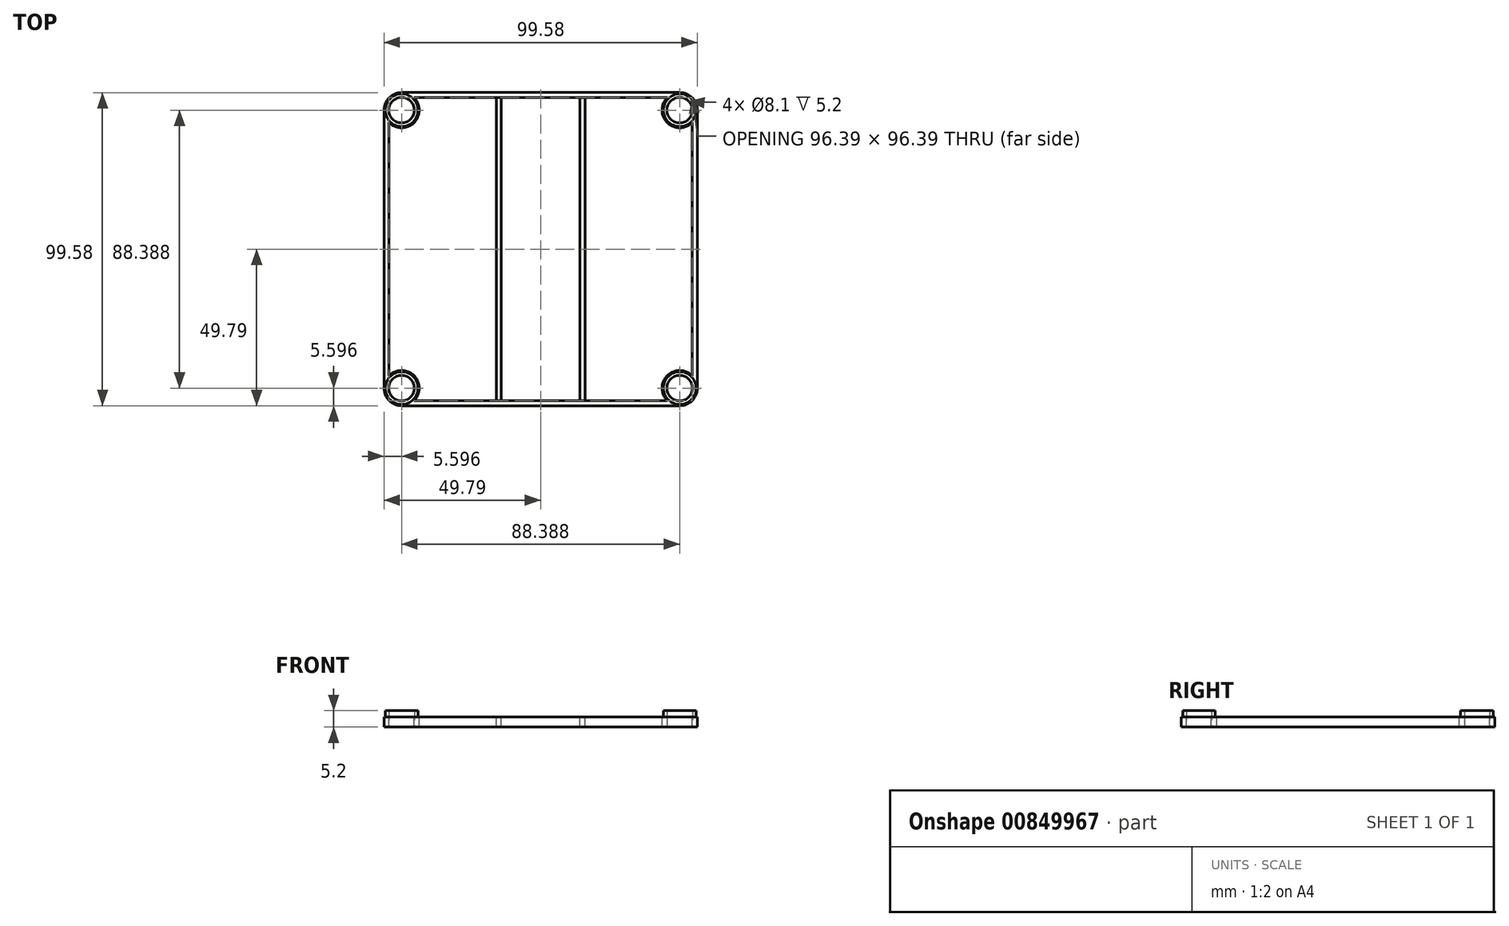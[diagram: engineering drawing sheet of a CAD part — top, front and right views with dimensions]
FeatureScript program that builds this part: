
annotation { "Feature Type Name" : "Feature", "Feature Type Description" : "" }
export const myFeature = defineFeature(function(context is Context, id is Id, definition is map)
    precondition{}
    {
        {
            var Q0;
            Q0=qCreatedBy(makeId("Top.planeOp"),FACE);
            var sketch = newSketch(context, id + "F0", { "sketchPlane" : qUnion([Q0])});
            skLineSegment(sketch, "E0.bottom", {"start": v(44.2, 44.2) * mm, "end": v(-44.2, 44.2) * mm, "construction": true});
            skLineSegment(sketch, "E0.top", {"start": v(44.2, -44.2) * mm, "end": v(-44.2, -44.2) * mm, "construction": true});
            skLineSegment(sketch, "E0.left", {"start": v(44.2, 44.2) * mm, "end": v(44.2, -44.2) * mm, "construction": true});
            skLineSegment(sketch, "E0.right", {"start": v(-44.2, 44.2) * mm, "end": v(-44.2, -44.2) * mm, "construction": true});
            skPoint(sketch, "E0.middle", {"position": v(0, 0) * mm});
            skLineSegment(sketch, "E1", {"start": v(-44.2, -44.2) * mm, "end": v(44.2, 44.2) * mm, "construction": true});
            skCircle(sketch, "E2", {"center": v(44.2, 44.2) * mm, "radius": 4 * mm, "construction": true});
            skCircle(sketch, "E3", {"center": v(-44.2, 44.2) * mm, "radius": 4 * mm, "construction": true});
            skCircle(sketch, "E4", {"center": v(-44.2, -44.2) * mm, "radius": 4 * mm, "construction": true});
            skCircle(sketch, "E5", {"center": v(44.2, -44.2) * mm, "radius": 4 * mm, "construction": true});
            skCircle(sketch, "E6", {"center": v(44.2, 44.2) * mm, "radius": 32.5 * mm, "construction": true});
            skCircle(sketch, "E7", {"center": v(-44.2, 44.2) * mm, "radius": 32.5 * mm, "construction": true});
            skCircle(sketch, "E8", {"center": v(-44.2, -44.2) * mm, "radius": 32.5 * mm, "construction": true});
            skCircle(sketch, "E9", {"center": v(44.2, -44.2) * mm, "radius": 32.5 * mm, "construction": true});
            skSolve(sketch);
        }
        {
            var Q0;
            Q0=qCreatedBy(makeId("Front.planeOp"),FACE);
            var sketch = newSketch(context, id + "F1", { "sketchPlane" : qUnion([Q0])});
            skLineSegment(sketch, "E10", {"start": v(0, 0) * mm, "end": v(0, 0.6) * mm});
            skLineSegment(sketch, "E11", {"start": v(0, 0.6) * mm, "end": v(0, 3.2) * mm});
            skLineSegment(sketch, "E12", {"start": v(0, 3.2) * mm, "end": v(0, 5.2) * mm});
            skSolve(sketch);
        }
        {
            var Q0;
            Q0=qCreatedBy(makeId("Top.planeOp"),FACE);
            var sketch = newSketch(context, id + "F2", { "sketchPlane" : qUnion([Q0])});
            skCircle(sketch, "E13.0", {"center": v(44.2, 44.2) * mm, "radius": 5.6 * mm, "construction": true});
            skPoint(sketch, "E14.center", {"position": v(0, 0) * mm});
            skLineSegment(sketch, "E15", {"start": v(44.2, 49.8) * mm, "end": v(0, 49.8) * mm});
            skLineSegment(sketch, "E16", {"start": v(49.8, 44.2) * mm, "end": v(49.8, 0) * mm});
            skArc(sketch, "E17", {"start": v(44.2, 49.8) * mm, "mid": v(48.15, 48.15) * mm, "end": v(49.8, 44.2) * mm});
            skCircle(sketch, "E18.0", {"center": v(44.2, 44.2) * mm, "radius": 4 * mm, "construction": true});
            skLineSegment(sketch, "E19", {"start": v(44.2, 48.2) * mm, "end": v(40.27, 48.2) * mm, "construction": true});
            skLineSegment(sketch, "E20", {"start": v(48.2, 44.2) * mm, "end": v(48.2, 40.27) * mm, "construction": true});
            skLineSegment(sketch, "E21", {"start": v(40.27, 48.2) * mm, "end": v(0, 48.2) * mm});
            skLineSegment(sketch, "E22", {"start": v(48.2, 40.27) * mm, "end": v(48.2, 0) * mm});
            skArc(sketch, "E23", {"start": v(40.27, 48.2) * mm, "mid": v(40.23, 40.23) * mm, "end": v(48.2, 40.27) * mm});
            skArc(sketch, "E24.1.0", {"start": v(-48.2, 40.27) * mm, "mid": v(-40.23, 40.23) * mm, "end": v(-40.27, 48.2) * mm});
            skLineSegment(sketch, "E24.1.1", {"start": v(-48.2, 40.27) * mm, "end": v(-48.2, 0) * mm});
            skLineSegment(sketch, "E24.1.2", {"start": v(-49.8, 44.2) * mm, "end": v(-49.8, 0) * mm});
            skLineSegment(sketch, "E24.1.3", {"start": v(-40.27, 48.2) * mm, "end": v(0, 48.2) * mm});
            skLineSegment(sketch, "E24.1.4", {"start": v(-44.2, 49.8) * mm, "end": v(0, 49.8) * mm});
            skArc(sketch, "E24.1.5", {"start": v(-49.8, 44.2) * mm, "mid": v(-48.15, 48.15) * mm, "end": v(-44.2, 49.8) * mm});
            skArc(sketch, "E24.2.0", {"start": v(-40.27, -48.2) * mm, "mid": v(-40.23, -40.23) * mm, "end": v(-48.2, -40.27) * mm});
            skLineSegment(sketch, "E24.2.1", {"start": v(-40.27, -48.2) * mm, "end": v(0, -48.2) * mm});
            skLineSegment(sketch, "E24.2.2", {"start": v(-44.2, -49.8) * mm, "end": v(0, -49.8) * mm});
            skLineSegment(sketch, "E24.2.3", {"start": v(-48.2, -40.27) * mm, "end": v(-48.2, 0) * mm});
            skLineSegment(sketch, "E24.2.4", {"start": v(-49.8, -44.2) * mm, "end": v(-49.8, 0) * mm});
            skArc(sketch, "E24.2.5", {"start": v(-44.2, -49.8) * mm, "mid": v(-48.15, -48.15) * mm, "end": v(-49.8, -44.2) * mm});
            skArc(sketch, "E24.3.0", {"start": v(48.2, -40.27) * mm, "mid": v(40.23, -40.23) * mm, "end": v(40.27, -48.2) * mm});
            skLineSegment(sketch, "E24.3.1", {"start": v(48.2, -40.27) * mm, "end": v(48.2, 0) * mm});
            skLineSegment(sketch, "E24.3.2", {"start": v(49.8, -44.2) * mm, "end": v(49.8, 0) * mm});
            skLineSegment(sketch, "E24.3.3", {"start": v(40.27, -48.2) * mm, "end": v(0, -48.2) * mm});
            skLineSegment(sketch, "E24.3.4", {"start": v(44.2, -49.8) * mm, "end": v(0, -49.8) * mm});
            skArc(sketch, "E24.3.5", {"start": v(49.8, -44.2) * mm, "mid": v(48.15, -48.15) * mm, "end": v(44.2, -49.8) * mm});
            skSolve(sketch);
        }
        {
            var Q0;
            Q0=qCreatedBy(makeId("Top.planeOp"),FACE);
            var sketch = newSketch(context, id + "F3", { "sketchPlane" : qUnion([Q0])});
            skLineSegment(sketch, "E25.0.0", {"start": v(0, -48.2) * mm, "end": v(40.27, -48.2) * mm, "construction": true});
            skArc(sketch, "E25.0.1", {"start": v(40.27, -48.2) * mm, "mid": v(40.23, -40.23) * mm, "end": v(48.2, -40.27) * mm, "construction": true});
            skLineSegment(sketch, "E25.0.2", {"start": v(48.2, -40.27) * mm, "end": v(48.2, 0) * mm, "construction": true});
            skLineSegment(sketch, "E25.0.3", {"start": v(48.2, 0) * mm, "end": v(48.2, 40.27) * mm, "construction": true});
            skArc(sketch, "E25.0.4", {"start": v(48.2, 40.27) * mm, "mid": v(40.23, 40.23) * mm, "end": v(40.27, 48.2) * mm, "construction": true});
            skLineSegment(sketch, "E25.0.5", {"start": v(40.27, 48.2) * mm, "end": v(0, 48.2) * mm, "construction": true});
            skLineSegment(sketch, "E25.0.6", {"start": v(0, 48.2) * mm, "end": v(-40.27, 48.2) * mm, "construction": true});
            skArc(sketch, "E25.0.7", {"start": v(-40.27, 48.2) * mm, "mid": v(-40.23, 40.23) * mm, "end": v(-48.2, 40.27) * mm, "construction": true});
            skLineSegment(sketch, "E25.0.8", {"start": v(-48.2, 40.27) * mm, "end": v(-48.2, 0) * mm, "construction": true});
            skLineSegment(sketch, "E25.0.9", {"start": v(-48.2, 0) * mm, "end": v(-48.2, -40.27) * mm, "construction": true});
            skArc(sketch, "E25.0.10", {"start": v(-48.2, -40.27) * mm, "mid": v(-40.23, -40.23) * mm, "end": v(-40.27, -48.2) * mm, "construction": true});
            skLineSegment(sketch, "E25.0.11", {"start": v(-40.27, -48.2) * mm, "end": v(0, -48.2) * mm, "construction": true});
            skLineSegment(sketch, "E26.bottom", {"start": v(12.5, 48.2) * mm, "end": v(-12.5, 48.2) * mm});
            skLineSegment(sketch, "E26.top", {"start": v(12.5, -48.2) * mm, "end": v(-12.5, -48.2) * mm});
            skLineSegment(sketch, "E26.left", {"start": v(12.5, 48.2) * mm, "end": v(12.5, -48.2) * mm});
            skLineSegment(sketch, "E26.right", {"start": v(-12.5, 48.2) * mm, "end": v(-12.5, -48.2) * mm});
            skPoint(sketch, "E26.middle", {"position": v(0, 0) * mm});
            skLineSegment(sketch, "E27", {"start": v(-12.5, -48.2) * mm, "end": v(-14.1, -48.2) * mm});
            skLineSegment(sketch, "E28", {"start": v(-14.1, -48.2) * mm, "end": v(-14.1, 48.2) * mm});
            skLineSegment(sketch, "E29", {"start": v(-14.1, 48.2) * mm, "end": v(-12.5, 48.2) * mm});
            skLineSegment(sketch, "E30", {"start": v(12.5, 48.2) * mm, "end": v(14.1, 48.2) * mm});
            skLineSegment(sketch, "E31", {"start": v(14.1, 48.2) * mm, "end": v(14.1, -48.2) * mm});
            skLineSegment(sketch, "E32", {"start": v(14.1, -48.2) * mm, "end": v(12.5, -48.2) * mm});
            skSolve(sketch);
        }
        {
            var Q0;
            Q0=qCreatedBy(makeId("Top.planeOp"),FACE);
            var sketch = newSketch(context, id + "F4", { "sketchPlane" : qUnion([Q0])});
            skCircle(sketch, "E33.0", {"center": v(44.2, 44.2) * mm, "radius": 5.2 * mm});
            skCircle(sketch, "E34.1.0", {"center": v(-44.2, 44.2) * mm, "radius": 5.2 * mm});
            skCircle(sketch, "E34.2.0", {"center": v(-44.2, -44.2) * mm, "radius": 5.2 * mm});
            skCircle(sketch, "E34.3.0", {"center": v(44.2, -44.2) * mm, "radius": 5.2 * mm});
            skPoint(sketch, "E34.center", {"position": v(0, 0) * mm});
            skSolve(sketch);
        }
        {
            var Q0;
            Q0=qCreatedBy(makeId("Top.planeOp"),FACE);
            var sketch = newSketch(context, id + "F5", { "sketchPlane" : qUnion([Q0])});
            skCircle(sketch, "E35.0", {"center": v(44.2, 44.2) * mm, "radius": 4.05 * mm});
            skCircle(sketch, "E36.0", {"center": v(-44.2, 44.2) * mm, "radius": 4.05 * mm});
            skCircle(sketch, "E37.0", {"center": v(-44.2, -44.2) * mm, "radius": 4.05 * mm});
            skCircle(sketch, "E38.0", {"center": v(44.2, -44.2) * mm, "radius": 4.05 * mm});
            skSolve(sketch);
        }
        {
            var Q0;
            Q0 = qSketchRegion(id + "F2", true);
            var Q1;
            Q1=makeQuery(id+"F3.imprint","IMPRINT",FACE,{"disambiguationData":[TD([[makeQuery(id+"F3.imprint","IMPRINT",EDGE,{"derivedFrom":sQuery(id+"F3.wireOp",EDGE,"E26.right")}),-1.0]])]});
            var Q2;
            Q2=makeQuery(id+"F3.imprint","IMPRINT",FACE,{"disambiguationData":[TD([[makeQuery(id+"F3.imprint","IMPRINT",EDGE,{"derivedFrom":sQuery(id+"F3.wireOp",EDGE,"E26.left")}),1.0]])]});
            var Q3;
            Q3=sQuery(id+"F1.wireOp",EDGE,"E10");
            var Q4;
            Q4=sQuery(id+"F1.wireOp",EDGE,"E11");
            sweep(context, id + "F6", {"profiles" : qUnion([Q0, Q1, Q2]), "path" : qUnion([Q3, Q4])});
        }
        {
            var Q0;
            Q0 = qSketchRegion(id + "F4", true);
            var Q1;
            Q1=sQuery(id+"F1.wireOp",EDGE,"E10");
            var Q2;
            Q2=sQuery(id+"F1.wireOp",EDGE,"E11");
            var Q3;
            Q3=sQuery(id+"F1.wireOp",EDGE,"E12");
            sweep(context, id + "F7", {"operationType" : NewBodyOperationType.ADD, "profiles" : qUnion([Q0]), "path" : qUnion([Q1, Q2, Q3])});
        }
        {
            var Q0;
            Q0 = qSketchRegion(id + "F5", true);
            extrude(context, id + "F8", {"entities" : qUnion([Q0]), "operationType" : NewBodyOperationType.REMOVE, "endBound" : BoundingType.THROUGH_ALL, "depth" : 25 * mm, "offsetDistance" : 25 * mm});
        }
    });
